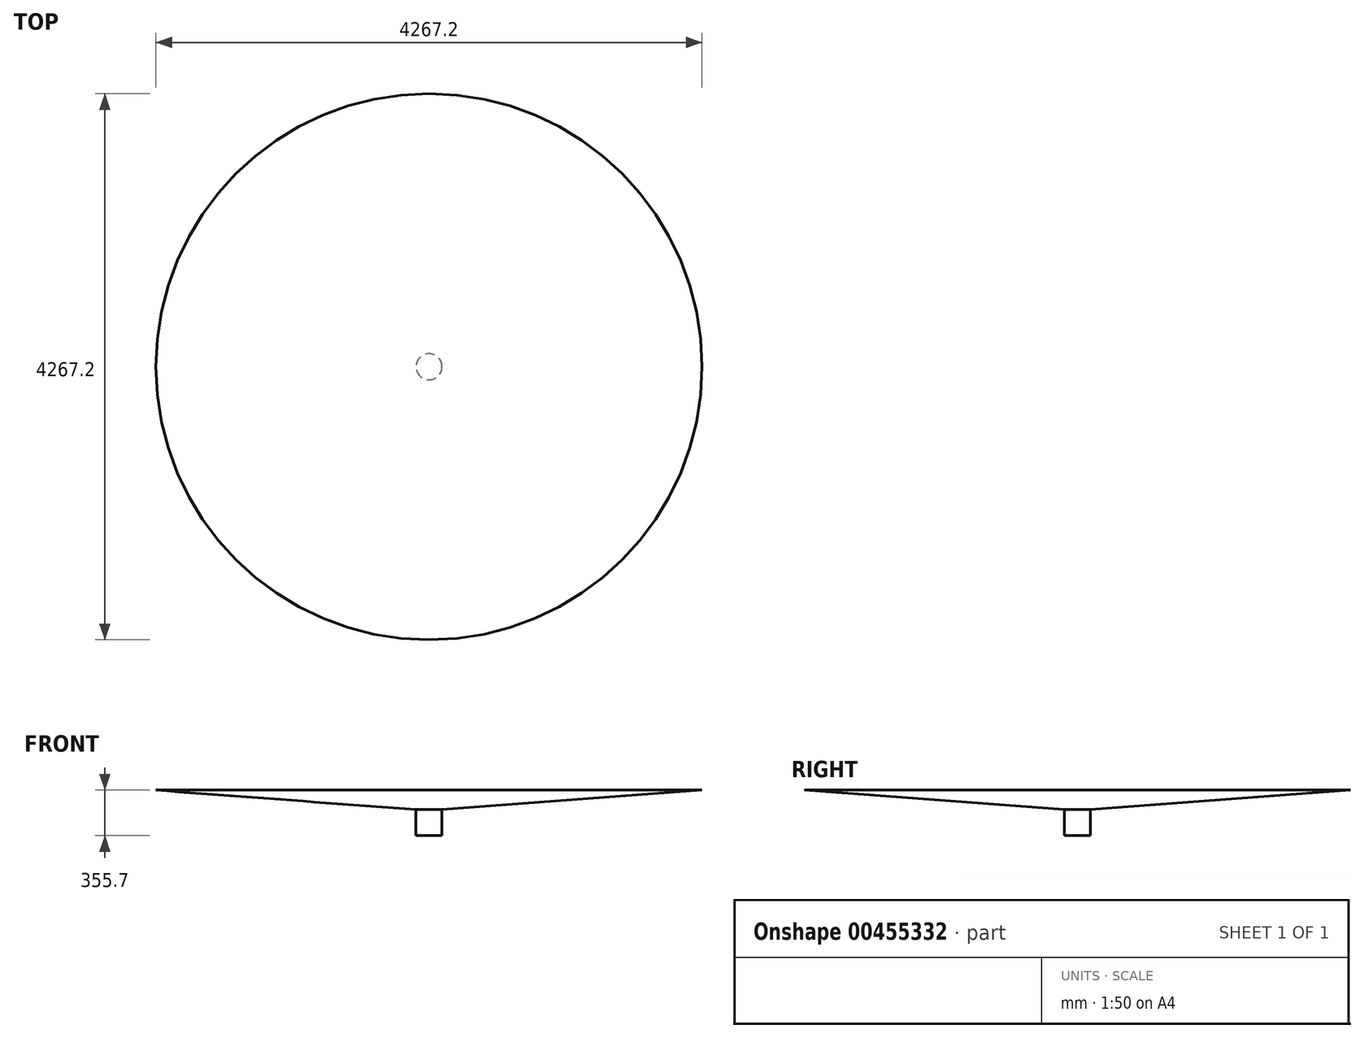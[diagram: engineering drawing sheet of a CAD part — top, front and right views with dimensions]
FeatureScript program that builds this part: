
annotation { "Feature Type Name" : "Feature", "Feature Type Description" : "" }
export const myFeature = defineFeature(function(context is Context, id is Id, definition is map)
    precondition{}
    {
        {
            var Q0;
            Q0=qCreatedBy(makeId("Front.planeOp"),FACE);
            var sketch = newSketch(context, id + "F0", { "sketchPlane" : qUnion([Q0])});
            skLineSegment(sketch, "E0", {"start": v(0, 0) * mm, "end": v(0, 1270.1) * mm, "construction": true});
            skLineSegment(sketch, "E1", {"start": v(0, 1270.1) * mm, "end": v(2133.6, 1270.1) * mm});
            skLineSegment(sketch, "E2", {"start": v(0, 914.4) * mm, "end": v(101.6, 914.4) * mm, "construction": true});
            skLineSegment(sketch, "E3", {"start": v(101.6, 1016) * mm, "end": v(0, 1016) * mm, "construction": true});
            skLineSegment(sketch, "E4", {"start": v(0, 1117.6) * mm, "end": v(101.6, 1117.6) * mm, "construction": true});
            skLineSegment(sketch, "E5", {"start": v(2133.6, 1270.1) * mm, "end": v(101.6, 1117.6) * mm});
            skLineSegment(sketch, "E6", {"start": v(0, 1117.6) * mm, "end": v(101.6, 1117.6) * mm});
            skLineSegment(sketch, "E7", {"start": v(0, 1016) * mm, "end": v(101.6, 1016) * mm});
            skLineSegment(sketch, "E8", {"start": v(0, 914.4) * mm, "end": v(101.6, 914.4) * mm});
            skLineSegment(sketch, "E9", {"start": v(101.6, 1117.6) * mm, "end": v(101.6, 914.4) * mm});
            skLineSegment(sketch, "E10", {"start": v(0, 1270.1) * mm, "end": v(0, 914.4) * mm});
            skSolve(sketch);
        }
        {
            var Q0;
            {var subQ0=sQuery(id+"F0.wireOp",EDGE,"E1");Q0=makeQuery(id+"F0.imprint","IMPRINT",FACE,{"disambiguationData":[TD([[makeQuery(id+"F0.imprint","IMPRINT",EDGE,{"derivedFrom":subQ0}),-1.0]])]});}
            var Q1;
            {var subQ0=sQuery(id+"F0.wireOp",EDGE,"E6");Q1=makeQuery(id+"F0.imprint","IMPRINT",FACE,{"disambiguationData":[TD([[makeQuery(id+"F0.imprint","IMPRINT",EDGE,{"derivedFrom":subQ0}),-1.0]])]});}
            var Q2;
            {var subQ0=sQuery(id+"F0.wireOp",EDGE,"E7");Q2=makeQuery(id+"F0.imprint","IMPRINT",FACE,{"disambiguationData":[TD([[makeQuery(id+"F0.imprint","IMPRINT",EDGE,{"derivedFrom":subQ0}),-1.0]])]});}
            var Q3;
            Q3=sQuery(id+"F0.wireOp",EDGE,"E0");
            revolve(context, id + "F1", {"surfaceOperationType" : NewSurfaceOperationType.NEW, "entities" : qUnion([Q0, Q1, Q2]), "axis" : qUnion([Q3]), "revolveType" : RevolveType.FULL});
        }
    });
